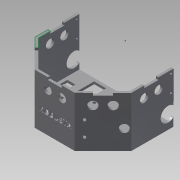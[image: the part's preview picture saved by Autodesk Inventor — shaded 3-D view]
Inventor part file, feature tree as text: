
AUTODESK INVENTOR PART (.ipt)
format: ipt  version: 2015 SP1 (Build 190203100, 203)  size: 684,032 bytes
history: native  units: mm
features: extrude x28, reference x24, sketch x23, projected_geometry x11
ambient origin geometry x8: Origin, YZ Plane, XZ Plane, XY Plane, X Axis, Y Axis, Z Axis, Center Point
bodies: Body1 (feature_tree)
feature tree (86):
  sketch  "Sketch1"  dims[d64=3.0mm d65=0.0mm d68=60.0mm d69=0.0mm]
  extrude  "Extrusion8"  Depth=60.0mm TaperAngle=0.0deg
  extrude  "Extrusion9"  Depth=3.5mm
  extrude  "Extrusion10"  Depth=3.5mm
  extrude  "Extrusion11"  Depth=3.5mm
  extrude  "Extrusion12"  Depth=10.0mm
  extrude  "Extrusion19"  Depth=17.5mm
  extrude  "Extrusion22"  Depth=17.5mm
  extrude  "Extrusion23"  Depth=10.0mm
  sketch  "Sketch22"  dims[d141=10.0mm d144=1.65mm]
  extrude  "Extrusion27"  Depth=10.0mm TaperAngle=0.0deg
  extrude  "Extrusion30"  Depth=3.5mm
  extrude  "Extrusion31"  Depth=7.0mm
  extrude  "Extrusion32"  Depth=7.0mm
  extrude  "Extrusion33"  Depth=10.0mm TaperAngle=0.0deg
  extrude  "Extrusion36"  Depth=17.5mm
  extrude  "Extrusion44"  Depth=3.0mm TaperAngle=0.0deg
  sketch  "Sketch40"  dims[d186=10.0mm d187=0.0mm d193=3.0mm d194=0.0mm]
  sketch  "Sketch41"  dims[d195=120.811657mm d198=50.041827mm]
  sketch  "Sketch42"  dims[d199=50.041827mm d200=50.041827mm]
  sketch  "Sketch43"  dims[d201=52.663858mm d202=52.663858mm]
  sketch  "Sketch44"  dims[d204=3.0mm d205=51.421217mm]
  extrude  "Extrusion46"  Depth=120.811657mm
  extrude  "Extrusion47"  Depth=50.041827mm
  extrude  "Extrusion48"  Depth=52.663858mm
  extrude  "Extrusion49"  Depth=3.0mm
  extrude  "Extrusion50"  Depth=47.556546mm
  extrude  "Extrusion51"  Depth=51.421217mm
  extrude  "Extrusion52"  TaperAngle=135.0deg  [1 undecoded]
  extrude  "Extrusion54"  TaperAngle=135.0deg  [1 undecoded]
  extrude  "Extrusion55"  TaperAngle=135.0deg  [1 undecoded]
  extrude  "Extrusion56"  TaperAngle=135.0deg  [1 undecoded]
  extrude  "Extrusion57"  TaperAngle=135.0deg  [1 undecoded]
  extrude  "Extrusion58"  TaperAngle=135.0deg  [1 undecoded]
  extrude  "Extrusion59"  Depth=3.0mm
  sketch  "Sketch10"  dims[d115=3.5mm d116=3.5mm]
  sketch  "Sketch11"  dims[d117=3.5mm d118=3.5mm]
  reference  "Reference28"
  reference  "Reference29"
  reference  "Reference30"
  reference  "Reference31"
  reference  "Reference32"
  reference  "Reference33"
  reference  "Reference34"
  sketch  "Sketch12"  dims[d119=3.5mm d120=3.5mm]
  reference  "Reference35"
  reference  "Reference36"
  sketch  "Sketch18"  dims[d127=10.0mm d128=0.0mm d129=10.0mm]
  sketch  "Sketch20"  dims[d130=17.5mm d132=17.5mm]
  reference  "Reference75"
  reference  "Reference76"
  sketch  "Sketch21"  dims[d133=15.0mm d136=17.5mm d137=10.0mm]
  sketch  "Sketch23"  dims[d145=10.0mm d146=0.0mm d147=10.0mm d148=0.0mm]
  reference  "Reference79"
  reference  "Reference80"
  reference  "Reference81"
  reference  "Reference82"
  sketch  "Sketch26"  dims[d161=3.5mm d162=3.5mm]
  reference  "Reference83"
  reference  "Reference84"
  reference  "Reference85"
  reference  "Reference86"
  reference  "Reference87"
  reference  "Reference88"
  reference  "Reference89"
  reference  "Reference90"
  projected_geometry  "Projected Loop2"
  sketch  "Sketch27"  dims[d163=7.0mm d164=7.0mm]
  sketch  "Sketch28"  dims[d165=7.0mm d166=7.0mm]
  projected_geometry  "Projected Loop3"
  sketch  "Sketch31"  dims[d167=10.0mm d168=0.0mm d173=10.0mm d174=0.0mm]
  sketch  "Sketch38"  dims[d175=10.0mm d176=0.0mm d181=17.5mm]
  reference  "Reference129"
  projected_geometry  "Projected Loop5"
  projected_geometry  "Projected Loop6"
  projected_geometry  "Projected Loop7"
  sketch  "Sketch46"  dims[d206=47.556546mm d207=47.556546mm]
  sketch  "Sketch47"  dims[d208=47.556546mm d209=51.421217mm]
  projected_geometry  "Projected Loop9"
  sketch  "Sketch48"  dims[d210=135.0deg d211=135.0deg]
  projected_geometry  "Projected Loop10"
  projected_geometry  "Projected Loop11"
  projected_geometry  "Projected Loop12"
  projected_geometry  "Projected Loop13"
  projected_geometry  "Projected Loop14"
  sketch  "Sketch49"  dims[d212=135.0deg d213=135.0deg d214=135.0deg d215=135.0deg d216=135.0deg d217=135.0deg d218=3.0mm d219=3.0mm d220=3.0mm d221=3.0mm d222=0.0mm d223=17.500137mm d225=3.0mm d231=0.0mm d232=3.0mm d233=0.0mm d234=3.0mm d235=0.0mm d236=3.0mm d237=0.0mm d242=3.5mm d243=3.5mm d244=10.0mm d245=0.0mm d260=180.0mm d261=0.0mm d262=3.5mm d263=3.5mm d270=10.25mm d271=10.25mm d272=18.0mm d273=9.0mm d276=10.25mm d277=10.25mm d278=9.0mm d279=9.0mm d282=10.25mm d283=10.25mm d284=18.0mm d285=9.0mm d289=10.25mm d290=10.25mm d291=18.0mm d292=9.0mm d293=3.5mm d294=3.5mm d295=18.75mm d296=29.25mm d297=8.542mm d298=3.5mm d299=3.5mm d300=8.542mm d301=8.542mm d302=18.75mm d303=29.25mm d304=10.0mm d305=9.375mm d306=5.0mm d307=10.0mm d308=5.0mm d309=9.375mm d310=11.877277mm d311=6.0mm d312=6.0mm d313=10.0mm d314=0.0mm d315=10.0mm d316=0.0mm d317=10.0mm d318=0.0mm d319=10.0mm d320=0.0mm d321=10.0mm d322=0.0mm d323=10.0mm d324=0.0mm d325=10.0mm d326=0.0mm d329=10.0mm d330=5.0mm d331=10.0mm d332=10.0mm d333=0.0mm d334=10.0mm d335=0.0mm d336=10.0mm d337=0.0mm d338=10.0mm d339=0.0mm d340=3.5mm d341=10.0mm d342=0.0mm d343=15.0mm d344=25.0mm d345=10.0mm d346=0.0mm]
note: 6 required parameter values undecoded (feature->parameter linkage not recoverable at this tier; creation-order binding heuristic only, values carry confidence <= 0.55)
